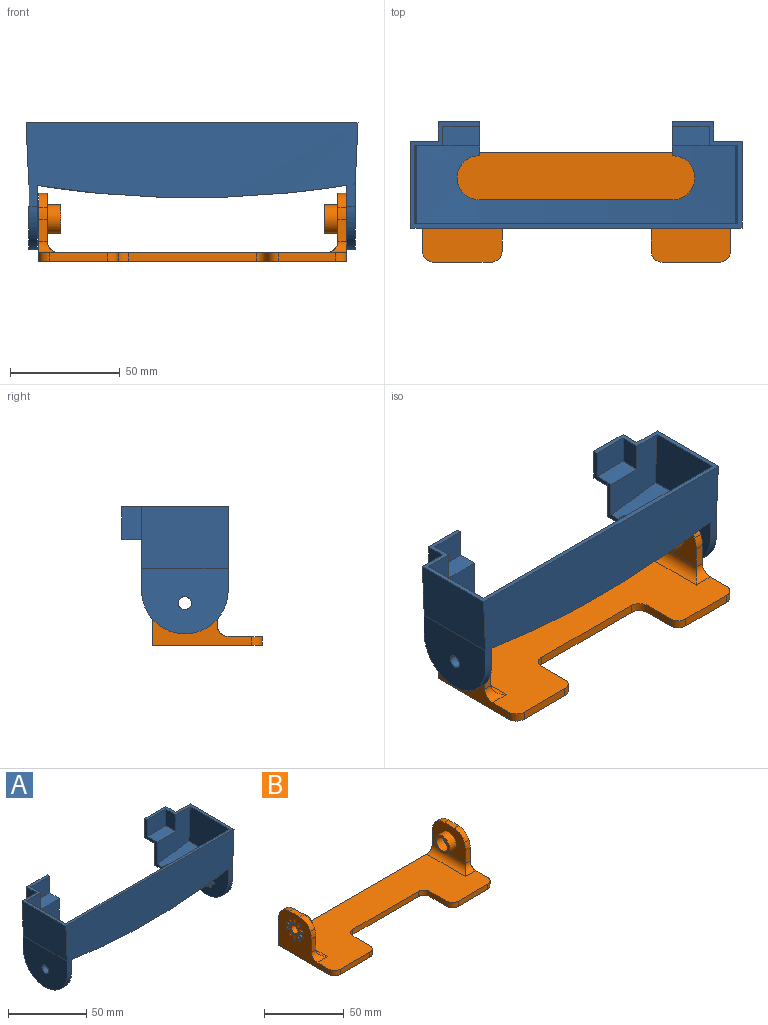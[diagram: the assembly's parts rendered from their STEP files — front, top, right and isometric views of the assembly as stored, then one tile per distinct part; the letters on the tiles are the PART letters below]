
ASSEMBLY  parts=2 mates=1
PART A: 142 faces, bbox 151.5x48.5x58 mm
  f0: cylinder r=443.67mm len=141mm, axis (0,1,0), area 2932.7mm2, adj f1,f32,f83,f84,f85,f86,f87,f88
  f1: plane 151.49x38.25mm, normal (0,-1,0), area 4905.7mm2, adj f0,f2,f21,f22,f23,f24,f26,f27
  f2: plane 151.49x48.5mm, normal (0,0,1), area 608.2mm2, adj f1,f3,f5,f7,f8,f10,f11,f12
  f3: plane 18.77x15mm, normal (0,1,0), area 281.5mm2, adj f2,f4,f20,f84
  f4: plane 18.77x9mm, normal (0,0,-1), area 168.9mm2, adj f3,f20,f83,f84
  f5: plane 16.77x13mm, normal (0,-1,0), area 218mm2, adj f2,f6,f7,f84
  f6: plane 16.77x9mm, normal (0,0,1), area 150.8mm2, adj f5,f7,f8,f84,f85
  f7: plane 13x9mm, normal (-1,0,0), area 117mm2, adj f2,f5,f6,f8
  f8: plane 30.03x29.76mm, normal (0,-1,0), area 605.6mm2, adj f2,f6,f7,f9,f10,f85
  f9: cylinder r=441.67mm len=145.15mm, axis (0,1,0), area 2691.9mm2, adj f8,f10,f11,f12,f13,f85,f86,f87
  f10: plane 35.5x26.2mm, normal (-1,0,0.04), area 931mm2, adj f2,f8,f9,f11
  f11: plane 147.48x32.25mm, normal (0,1,0), area 4422mm2, adj f2,f9,f10,f12
  f12: plane 35.5x26.3mm, normal (1,0,0.04), area 934.4mm2, adj f2,f9,f11,f13
  f13: plane 30.08x29.75mm, normal (0,-1,0), area 607.9mm2, adj f2,f9,f12,f14,f15,f89
  f14: plane 16.76x9mm, normal (0,0,1), area 150.8mm2, adj f13,f15,f16,f89
  f15: plane 13x9mm, normal (1,0,0), area 117mm2, adj f2,f13,f14,f16
  f16: plane 16.76x13mm, normal (0,-1,0), area 217.8mm2, adj f2,f14,f15,f89
  f17: plane 18.76x15mm, normal (0,1,0), area 281.3mm2, adj f2,f18,f19,f89
  f18: plane 18.76x9mm, normal (0,0,-1), area 168.8mm2, adj f17,f19,f89,f90
  f19: plane 15x9mm, normal (-1,0,0), area 135mm2, adj f2,f17,f18,f90
  f20: plane 15x9mm, normal (1,0,0), area 135mm2, adj f2,f3,f4,f83
  f21: plane 39.5x27.9mm, normal (1,0,-0.04), area 1103.2mm2, adj f1,f2,f22,f83
  f22: cylinder r=443.67mm len=39.5mm, axis (0,1,0), area 23.3mm2, adj f1,f21,f23,f83
  f23: plane 39.5x0.58mm, normal (0,0,1), area 23mm2, adj f1,f22,f24,f83
  f24: plane 39.5x30mm, normal (1,0,0), area 989.3mm2, adj f1,f23,f25,f26,f83
  f25: cylinder r=3mm len=6mm, axis (1,0,0), area 75.4mm2, adj f24,f32
  f26: cylinder r=19.75mm len=39.5mm, axis (1,0,0), area 248.2mm2, adj f1,f24,f32,f83
  f27: cylinder r=19.75mm len=39.5mm, axis (-1,0,0), area 248.2mm2, adj f1,f28,f90,f91
  f28: plane 39.5x30mm, normal (-1,0,0), area 989.3mm2, adj f1,f27,f29,f30,f90
  f29: cylinder r=3mm len=6mm, axis (-1,0,0), area 75.4mm2, adj f28,f91
  f30: plane 39.5x0mm, normal (0,0,1), area 0mm2, adj f28,f31
  f31: plane 39.5x28mm, normal (-1,0,-0.04), area 1107.1mm2, adj f1,f2,f30,f90
  f32: plane 39.5x29.43mm, normal (-1,0,0), area 904.1mm2, adj f0,f1,f25,f26,f33,f38,f43,f48
  f33: extruded ~4x2mm, area 1mm2, adj f32,f34,f35,f36,f37
  f34: bspline ~2x1.45mm, area 1.8mm2, adj f33,f35,f37
  f35: bspline ~3.07x1.23mm, area 2mm2, adj f33,f34,f36
  f36: bspline ~2x1.44mm, area 1.8mm2, adj f33,f35,f37
  f37: bspline ~3.1x1.26mm, area 2mm2, adj f33,f34,f36
  f38: extruded ~3.44x2.85mm, area 1mm2, adj f32,f39,f40,f41,f42
  f39: bspline ~1.73x1.43mm, area 1.8mm2, adj f38,f40,f42
  f40: bspline ~2.57x2.18mm, area 2mm2, adj f38,f39,f41
  f41: bspline ~1.73x1.43mm, area 1.8mm2, adj f38,f40,f42
  f42: bspline ~2.5x2.15mm, area 2mm2, adj f38,f39,f41
  f43: extruded ~3.85x2.27mm, area 1mm2, adj f32,f44,f45,f46,f47
  f44: bspline ~1.94x1.38mm, area 1.8mm2, adj f43,f45,f47
  f45: bspline ~2.9x1.68mm, area 2mm2, adj f43,f44,f46
  f46: bspline ~1.94x1.37mm, area 1.8mm2, adj f43,f45,f47
  f47: bspline ~2.77x1.63mm, area 2mm2, adj f43,f44,f46
  f48: extruded ~3.85x2.27mm, area 1mm2, adj f32,f49,f50,f51,f52
  f49: bspline ~1.94x1.38mm, area 1.8mm2, adj f48,f50,f52
  f50: bspline ~2.94x1.63mm, area 2mm2, adj f48,f49,f51
  f51: bspline ~1.94x1.37mm, area 1.8mm2, adj f48,f50,f52
  f52: bspline ~2.92x1.72mm, area 2mm2, adj f48,f49,f51
  f53: extruded ~3.44x2.85mm, area 1mm2, adj f32,f54,f55,f56,f57
  f54: bspline ~1.73x1.43mm, area 1.8mm2, adj f53,f55,f57
  f55: bspline ~2.57x2.22mm, area 2mm2, adj f53,f54,f56
  f56: bspline ~1.73x1.43mm, area 1.8mm2, adj f53,f55,f57
  f57: bspline ~2.62x2.17mm, area 2mm2, adj f53,f54,f56
  f58: extruded ~4x2mm, area 1mm2, adj f32,f59,f60,f61,f62
  f59: bspline ~2x1.45mm, area 1.8mm2, adj f58,f60,f62
  f60: bspline ~3.07x1.23mm, area 2mm2, adj f58,f59,f61
  f61: bspline ~2x1.44mm, area 1.8mm2, adj f58,f60,f62
  f62: bspline ~3.1x1.26mm, area 2mm2, adj f58,f59,f61
  f63: extruded ~3.44x2.85mm, area 1mm2, adj f32,f64,f65,f66,f67
  f64: bspline ~1.73x1.43mm, area 1.8mm2, adj f63,f65,f67
  f65: bspline ~2.57x2.18mm, area 2mm2, adj f63,f64,f66
  f66: bspline ~1.73x1.43mm, area 1.8mm2, adj f63,f65,f67
  f67: bspline ~2.58x2.26mm, area 2mm2, adj f63,f64,f66
  f68: extruded ~3.85x2.27mm, area 1mm2, adj f32,f69,f70,f71,f72
  f69: bspline ~1.94x1.38mm, area 1.8mm2, adj f68,f70,f72
  f70: bspline ~2.9x1.68mm, area 2mm2, adj f68,f69,f71
  f71: bspline ~1.94x1.37mm, area 1.8mm2, adj f68,f70,f72
  f72: bspline ~2.99x1.63mm, area 2mm2, adj f68,f69,f71
  f73: extruded ~3.85x2.27mm, area 1mm2, adj f32,f74,f75,f76,f77
  f74: bspline ~1.94x1.38mm, area 1.8mm2, adj f73,f75,f77
  f75: bspline ~2.94x1.63mm, area 2mm2, adj f73,f74,f76
  f76: bspline ~1.94x1.37mm, area 1.8mm2, adj f73,f75,f77
  f77: bspline ~2.92x1.72mm, area 2mm2, adj f73,f74,f76
  f78: extruded ~3.44x2.85mm, area 1mm2, adj f32,f79,f80,f81,f82
  f79: bspline ~1.73x1.43mm, area 1.8mm2, adj f78,f80,f82
  f80: bspline ~2.57x2.22mm, area 2mm2, adj f78,f79,f81
  f81: bspline ~1.73x1.43mm, area 1.8mm2, adj f78,f80,f82
  f82: bspline ~2.5x2.15mm, area 2mm2, adj f78,f79,f81
  f83: plane 38.25x31.76mm, normal (0,1,0), area 695.9mm2, adj f0,f2,f4,f20,f21,f22,f23,f24
  f84: plane 32.04x9mm, normal (-1,0,0), area 44mm2, adj f0,f2,f3,f4,f5,f6,f83,f85
  f85: plane 19.04x6.5mm, normal (-1,0,0), area 47.1mm2, adj f0,f6,f8,f9,f84,f86
  f86: cylinder r=10mm len=20mm, axis (0,0,1), area 65.1mm2, adj f0,f9,f85,f87
  f87: plane 87.83x4.19mm, normal (0,1,0), area 175.9mm2, adj f0,f9,f86,f88
  f88: cylinder r=10mm len=20mm, axis (0,0,1), area 63.8mm2, adj f0,f9,f87,f89
  f89: plane 32.09x15.5mm, normal (1,0,0), area 91.2mm2, adj f0,f2,f9,f13,f14,f16,f17,f18
  f90: plane 38.25x31.76mm, normal (0,1,0), area 698mm2, adj f0,f2,f18,f19,f27,f28,f31,f89
  f91: plane 39.5x29.34mm, normal (1,0,0), area 900.4mm2, adj f0,f1,f27,f29,f90,f92,f97,f102
  f92: extruded ~4x2mm, area 1mm2, adj f91,f93,f94,f95,f96
  f93: bspline ~3.07x1.23mm, area 2mm2, adj f92,f94,f96
  f94: bspline ~2x1.44mm, area 1.8mm2, adj f92,f93,f95
  f95: bspline ~3.1x1.26mm, area 2mm2, adj f92,f94,f96
  f96: bspline ~2x1.45mm, area 1.8mm2, adj f92,f93,f95
  f97: extruded ~3.44x2.85mm, area 1mm2, adj f91,f98,f99,f100,f101
  f98: bspline ~2.57x2.18mm, area 2mm2, adj f97,f99,f101
  f99: bspline ~1.73x1.43mm, area 1.8mm2, adj f97,f98,f100
  f100: bspline ~2.5x2.15mm, area 2mm2, adj f97,f99,f101
  f101: bspline ~1.73x1.43mm, area 1.8mm2, adj f97,f98,f100
  f102: extruded ~3.85x2.27mm, area 1mm2, adj f91,f103,f104,f105,f106
  f103: bspline ~2.9x1.68mm, area 2mm2, adj f102,f104,f106
  f104: bspline ~1.94x1.37mm, area 1.8mm2, adj f102,f103,f105
  f105: bspline ~2.77x1.63mm, area 2mm2, adj f102,f104,f106
  f106: bspline ~1.94x1.38mm, area 1.8mm2, adj f102,f103,f105
  f107: extruded ~3.85x2.27mm, area 1mm2, adj f91,f108,f109,f110,f111
  f108: bspline ~2.94x1.63mm, area 2mm2, adj f107,f109,f111
  f109: bspline ~1.94x1.37mm, area 1.8mm2, adj f107,f108,f110
  f110: bspline ~2.92x1.72mm, area 2mm2, adj f107,f109,f111
  f111: bspline ~1.94x1.38mm, area 1.8mm2, adj f107,f108,f110
  f112: extruded ~3.44x2.85mm, area 1mm2, adj f91,f113,f114,f115,f116
  f113: bspline ~2.57x2.22mm, area 2mm2, adj f112,f114,f116
  f114: bspline ~1.73x1.43mm, area 1.8mm2, adj f112,f113,f115
  f115: bspline ~2.62x2.17mm, area 2mm2, adj f112,f114,f116
  f116: bspline ~1.73x1.43mm, area 1.8mm2, adj f112,f113,f115
  f117: extruded ~4x2mm, area 1mm2, adj f91,f118,f119,f120,f121
  f118: bspline ~3.07x1.23mm, area 2mm2, adj f117,f119,f121
  f119: bspline ~2x1.44mm, area 1.8mm2, adj f117,f118,f120
  f120: bspline ~3.1x1.26mm, area 2mm2, adj f117,f119,f121
  f121: bspline ~2x1.45mm, area 1.8mm2, adj f117,f118,f120
  f122: extruded ~3.44x2.85mm, area 1mm2, adj f91,f123,f124,f125,f126
  f123: bspline ~2.57x2.18mm, area 2mm2, adj f122,f124,f126
  f124: bspline ~1.73x1.43mm, area 1.8mm2, adj f122,f123,f125
  f125: bspline ~2.58x2.26mm, area 2mm2, adj f122,f124,f126
  f126: bspline ~1.73x1.43mm, area 1.8mm2, adj f122,f123,f125
  f127: extruded ~3.85x2.27mm, area 1mm2, adj f91,f128,f129,f130,f131
  f128: bspline ~2.9x1.68mm, area 2mm2, adj f127,f129,f131
  f129: bspline ~1.94x1.37mm, area 1.8mm2, adj f127,f128,f130
  f130: bspline ~2.99x1.63mm, area 2mm2, adj f127,f129,f131
  f131: bspline ~1.94x1.38mm, area 1.8mm2, adj f127,f128,f130
  f132: extruded ~3.85x2.27mm, area 1mm2, adj f91,f133,f134,f135,f136
  f133: bspline ~2.94x1.63mm, area 2mm2, adj f132,f134,f136
  f134: bspline ~1.94x1.37mm, area 1.8mm2, adj f132,f133,f135
  f135: bspline ~2.92x1.72mm, area 2mm2, adj f132,f134,f136
  f136: bspline ~1.94x1.38mm, area 1.8mm2, adj f132,f133,f135
  f137: extruded ~3.44x2.85mm, area 1mm2, adj f91,f138,f139,f140,f141
  f138: bspline ~2.57x2.22mm, area 2mm2, adj f137,f139,f141
  f139: bspline ~1.73x1.43mm, area 1.8mm2, adj f137,f138,f140
  f140: bspline ~2.5x2.15mm, area 2mm2, adj f137,f139,f141
  f141: bspline ~1.73x1.43mm, area 1.8mm2, adj f137,f138,f140
PART B: 144 faces, bbox 140.5x50x31 mm
  f0: plane 10x10mm, normal (1,0,0), area 50.3mm2, adj f16,f141
  f1: plane 10x10mm, normal (-1,0,0), area 50.3mm2, adj f22,f138
  f2: plane 140.5x50mm, normal (0,0,1), area 4693.3mm2, adj f3,f4,f5,f6,f7,f8,f9,f10
  f3: plane 58x4mm, normal (0,-1,0), area 232mm2, adj f2,f11,f128,f133
  f4: plane 15x4mm, normal (-1,0,0), area 60mm2, adj f2,f11,f128,f129
  f5: plane 26.25x4mm, normal (0,-1,0), area 105mm2, adj f2,f11,f129,f130
  f6: plane 45x30.99mm, normal (1,0,0), area 841.2mm2, adj f2,f7,f11,f18,f19,f20,f21,f22
  f7: plane 140.5x19.24mm, normal (0,1,0), area 694.6mm2, adj f2,f6,f8,f11,f15,f17,f21,f23
  f8: plane 45x30.99mm, normal (-1,0,0), area 841.2mm2, adj f2,f7,f11,f12,f13,f14,f15,f16
  f9: plane 26.25x4mm, normal (0,-1,0), area 105mm2, adj f2,f11,f131,f132
  f10: plane 15x4mm, normal (1,0,0), area 60mm2, adj f2,f11,f132,f133
  f11: plane 140.5x50mm, normal (0,0,-1), area 5314.3mm2, adj f3,f4,f5,f6,f7,f8,f9,f10
  f12: plane 10.24x4mm, normal (0,-1,0), area 40.9mm2, adj f8,f13,f17,f127
  f13: cylinder r=14.75mm len=5.43mm, axis (1,0,0), area 22.3mm2, adj f8,f12,f17,f136
  f14: plane 8.83x4mm, normal (0,0,1), area 35.3mm2, adj f8,f17,f136,f137
  f15: cylinder r=14.75mm len=5.43mm, axis (1,0,0), area 22.3mm2, adj f7,f8,f17,f137
  f16: cylinder r=3mm len=6mm, axis (1,0,0), area 75.4mm2, adj f0,f8
  f17: plane 29.5x21.99mm, normal (1,0,0), area 466.7mm2, adj f7,f12,f13,f14,f15,f126,f136,f137
  f18: plane 10.24x4mm, normal (0,-1,0), area 40.9mm2, adj f6,f19,f23,f125
  f19: cylinder r=14.75mm len=5.43mm, axis (-1,0,0), area 22.3mm2, adj f6,f18,f23,f135
  f20: plane 8.83x4mm, normal (0,0,1), area 35.3mm2, adj f6,f23,f134,f135
  f21: cylinder r=14.75mm len=5.43mm, axis (-1,0,0), area 22.3mm2, adj f6,f7,f23,f134
  f22: cylinder r=3mm len=6mm, axis (-1,0,0), area 75.4mm2, adj f1,f6
  f23: plane 29.5x21.99mm, normal (-1,0,0), area 466.7mm2, adj f7,f18,f19,f20,f21,f124,f134,f135
  f24: extruded ~4x2mm, area 1mm2, adj f8,f70,f71,f72,f73
  f25: extruded ~3.44x2.85mm, area 1mm2, adj f8,f34,f35,f36,f37
  f26: extruded ~3.85x2.27mm, area 1mm2, adj f8,f38,f39,f40,f41
  f27: extruded ~3.85x2.27mm, area 1mm2, adj f8,f42,f43,f44,f45
  f28: extruded ~3.44x2.85mm, area 1mm2, adj f8,f46,f47,f48,f49
  f29: extruded ~4x2mm, area 1mm2, adj f8,f50,f51,f52,f53
  f30: extruded ~3.44x2.85mm, area 1mm2, adj f8,f54,f55,f56,f57
  f31: extruded ~3.85x2.27mm, area 1mm2, adj f8,f58,f59,f60,f61
  f32: extruded ~3.85x2.27mm, area 1mm2, adj f8,f62,f63,f64,f65
  f33: extruded ~3.44x2.85mm, area 1mm2, adj f8,f66,f67,f68,f69
  f34: bspline ~1.73x1.43mm, area 1.8mm2, adj f25,f35,f36
  f35: bspline ~2.57x2.18mm, area 2mm2, adj f25,f34,f37
  f36: bspline ~2.62x2.17mm, area 2mm2, adj f25,f34,f37
  f37: bspline ~1.73x1.43mm, area 1.8mm2, adj f25,f35,f36
  f38: bspline ~1.94x1.37mm, area 1.8mm2, adj f26,f39,f40
  f39: bspline ~2.89x1.68mm, area 2mm2, adj f26,f38,f41
  f40: bspline ~2.92x1.72mm, area 2mm2, adj f26,f38,f41
  f41: bspline ~1.94x1.38mm, area 1.8mm2, adj f26,f39,f40
  f42: bspline ~1.94x1.37mm, area 1.8mm2, adj f27,f43,f44
  f43: bspline ~2.94x1.63mm, area 2mm2, adj f27,f42,f45
  f44: bspline ~2.77x1.63mm, area 2mm2, adj f27,f42,f45
  f45: bspline ~1.94x1.38mm, area 1.8mm2, adj f27,f43,f44
  f46: bspline ~1.73x1.43mm, area 1.8mm2, adj f28,f47,f48
  f47: bspline ~2.57x2.22mm, area 2mm2, adj f28,f46,f49
  f48: bspline ~2.5x2.15mm, area 2mm2, adj f28,f46,f49
  f49: bspline ~1.73x1.43mm, area 1.8mm2, adj f28,f47,f48
  f50: bspline ~2x1.44mm, area 1.8mm2, adj f29,f51,f52
  f51: bspline ~3.07x1.23mm, area 2mm2, adj f29,f50,f53
  f52: bspline ~3.1x1.26mm, area 2mm2, adj f29,f50,f53
  f53: bspline ~2x1.45mm, area 1.8mm2, adj f29,f51,f52
  f54: bspline ~1.73x1.43mm, area 1.8mm2, adj f30,f55,f56
  f55: bspline ~2.57x2.18mm, area 2mm2, adj f30,f54,f57
  f56: bspline ~2.62x2.17mm, area 2mm2, adj f30,f54,f57
  f57: bspline ~1.73x1.43mm, area 1.8mm2, adj f30,f55,f56
  f58: bspline ~1.94x1.37mm, area 1.8mm2, adj f31,f59,f60
  f59: bspline ~2.89x1.68mm, area 2mm2, adj f31,f58,f61
  f60: bspline ~2.92x1.72mm, area 2mm2, adj f31,f58,f61
  f61: bspline ~1.94x1.38mm, area 1.8mm2, adj f31,f59,f60
  f62: bspline ~1.94x1.37mm, area 1.8mm2, adj f32,f63,f64
  f63: bspline ~2.94x1.63mm, area 2mm2, adj f32,f62,f65
  f64: bspline ~2.77x1.63mm, area 2mm2, adj f32,f62,f65
  f65: bspline ~1.94x1.38mm, area 1.8mm2, adj f32,f63,f64
  f66: bspline ~1.73x1.43mm, area 1.8mm2, adj f33,f67,f68
  f67: bspline ~2.57x2.22mm, area 2mm2, adj f33,f66,f69
  f68: bspline ~2.58x2.26mm, area 2mm2, adj f33,f66,f69
  f69: bspline ~1.73x1.43mm, area 1.8mm2, adj f33,f67,f68
  f70: bspline ~2x1.44mm, area 1.8mm2, adj f24,f71,f72
  f71: bspline ~3.07x1.23mm, area 2mm2, adj f24,f70,f73
  f72: bspline ~3.1x1.26mm, area 2mm2, adj f24,f70,f73
  f73: bspline ~2x1.45mm, area 1.8mm2, adj f24,f71,f72
  f74: extruded ~3.85x2.27mm, area 1mm2, adj f6,f120,f121,f122,f123
  f75: extruded ~3.44x2.85mm, area 1mm2, adj f6,f84,f85,f86,f87
  f76: extruded ~3.85x2.27mm, area 1mm2, adj f6,f116,f117,f118,f119
  f77: extruded ~3.44x2.85mm, area 1mm2, adj f6,f112,f113,f114,f115
  f78: extruded ~4x2mm, area 1mm2, adj f6,f108,f109,f110,f111
  f79: extruded ~3.44x2.85mm, area 1mm2, adj f6,f104,f105,f106,f107
  f80: extruded ~3.85x2.27mm, area 1mm2, adj f6,f100,f101,f102,f103
  f81: extruded ~3.85x2.27mm, area 1mm2, adj f6,f96,f97,f98,f99
  f82: extruded ~3.44x2.85mm, area 1mm2, adj f6,f92,f93,f94,f95
  f83: extruded ~4x2mm, area 1mm2, adj f6,f88,f89,f90,f91
  f84: bspline ~1.73x1.43mm, area 1.8mm2, adj f75,f85,f86
  f85: bspline ~2.57x2.18mm, area 2mm2, adj f75,f84,f87
  f86: bspline ~2.62x2.17mm, area 2mm2, adj f75,f84,f87
  f87: bspline ~1.73x1.43mm, area 1.8mm2, adj f75,f85,f86
  f88: bspline ~2x1.44mm, area 1.8mm2, adj f83,f89,f90
  f89: bspline ~3.07x1.23mm, area 2mm2, adj f83,f88,f91
  f90: bspline ~3.1x1.26mm, area 2mm2, adj f83,f88,f91
  f91: bspline ~2x1.45mm, area 1.8mm2, adj f83,f89,f90
  f92: bspline ~1.73x1.43mm, area 1.8mm2, adj f82,f93,f94
  f93: bspline ~2.57x2.22mm, area 2mm2, adj f82,f92,f95
  f94: bspline ~2.5x2.15mm, area 2mm2, adj f82,f92,f95
  f95: bspline ~1.73x1.43mm, area 1.8mm2, adj f82,f93,f94
  f96: bspline ~1.94x1.37mm, area 1.8mm2, adj f81,f97,f98
  f97: bspline ~2.94x1.63mm, area 2mm2, adj f81,f96,f99
  f98: bspline ~2.99x1.63mm, area 2mm2, adj f81,f96,f99
  f99: bspline ~1.94x1.38mm, area 1.8mm2, adj f81,f97,f98
  f100: bspline ~1.94x1.37mm, area 1.8mm2, adj f80,f101,f102
  f101: bspline ~2.89x1.68mm, area 2mm2, adj f80,f100,f103
  f102: bspline ~2.92x1.72mm, area 2mm2, adj f80,f100,f103
  f103: bspline ~1.94x1.38mm, area 1.8mm2, adj f80,f101,f102
  f104: bspline ~1.73x1.43mm, area 1.8mm2, adj f79,f105,f106
  f105: bspline ~2.57x2.18mm, area 2mm2, adj f79,f104,f107
  f106: bspline ~2.62x2.17mm, area 2mm2, adj f79,f104,f107
  f107: bspline ~1.73x1.43mm, area 1.8mm2, adj f79,f105,f106
  f108: bspline ~2x1.44mm, area 1.8mm2, adj f78,f109,f110
  f109: bspline ~3.07x1.23mm, area 2mm2, adj f78,f108,f111
  f110: bspline ~3.1x1.26mm, area 2mm2, adj f78,f108,f111
  f111: bspline ~2x1.45mm, area 1.8mm2, adj f78,f109,f110
  f112: bspline ~1.73x1.43mm, area 1.8mm2, adj f77,f113,f114
  f113: bspline ~2.57x2.22mm, area 2mm2, adj f77,f112,f115
  f114: bspline ~2.58x2.26mm, area 2mm2, adj f77,f112,f115
  f115: bspline ~1.73x1.43mm, area 1.8mm2, adj f77,f113,f114
  f116: bspline ~1.94x1.37mm, area 1.8mm2, adj f76,f117,f118
  f117: bspline ~2.94x1.63mm, area 2mm2, adj f76,f116,f119
  f118: bspline ~2.99x1.63mm, area 2mm2, adj f76,f116,f119
  f119: bspline ~1.94x1.38mm, area 1.8mm2, adj f76,f117,f118
  f120: bspline ~1.94x1.37mm, area 1.8mm2, adj f74,f121,f122
  f121: bspline ~2.89x1.68mm, area 2mm2, adj f74,f120,f123
  f122: bspline ~2.92x1.72mm, area 2mm2, adj f74,f120,f123
  f123: bspline ~1.94x1.38mm, area 1.8mm2, adj f74,f121,f122
  f124: cylinder r=5mm len=34.5mm, axis (0,1,0), area 251.3mm2, adj f2,f7,f23,f125
  f125: cylinder r=5mm len=9mm, axis (-1,0,0), area 51.1mm2, adj f2,f6,f18,f124
  f126: cylinder r=5mm len=34.5mm, axis (0,-1,0), area 251.3mm2, adj f2,f7,f17,f127
  f127: cylinder r=5mm len=9mm, axis (-1,0,0), area 51.1mm2, adj f2,f8,f12,f126
  f128: cylinder r=5mm len=5mm, axis (0,0,1), area 31.4mm2, adj f2,f3,f4,f11
  f129: cylinder r=5mm len=5mm, axis (0,0,1), area 31.4mm2, adj f2,f4,f5,f11
  f130: cylinder r=5mm len=5mm, axis (0,0,1), area 31.4mm2, adj f2,f5,f6,f11
  f131: cylinder r=5mm len=5mm, axis (0,0,-1), area 31.4mm2, adj f2,f8,f9,f11
  f132: cylinder r=5mm len=5mm, axis (0,0,-1), area 31.4mm2, adj f2,f9,f10,f11
  f133: cylinder r=5mm len=5mm, axis (0,0,-1), area 31.4mm2, adj f2,f3,f10,f11
  f134: cylinder r=10mm len=9.3mm, axis (-1,0,0), area 47.7mm2, adj f6,f20,f21,f23
  f135: cylinder r=10mm len=9.3mm, axis (-1,0,0), area 47.7mm2, adj f6,f19,f20,f23
  f136: cylinder r=10mm len=9.3mm, axis (1,0,0), area 47.7mm2, adj f8,f13,f14,f17
  f137: cylinder r=10mm len=9.3mm, axis (1,0,0), area 47.7mm2, adj f8,f14,f15,f17
  f138: cylinder r=5mm len=10mm, axis (1,0,0), area 188.5mm2, adj f1,f140
  f139: cylinder r=6.5mm len=13mm, axis (1,0,0), area 245mm2, adj f23,f140
  f140: plane 13x13mm, normal (-1,0,0), area 54.2mm2, adj f138,f139
  f141: cylinder r=5mm len=10mm, axis (-1,0,0), area 188.5mm2, adj f0,f143
  f142: cylinder r=6.5mm len=13mm, axis (-1,0,0), area 245mm2, adj f17,f143
  f143: plane 13x13mm, normal (1,0,0), area 54.2mm2, adj f141,f142
PLACE A t=(-56.78,33.72,77.35)mm
PLACE B t=(-56.53,-5.28,-5.63)mm
MATE revolute A.f25 <-> B.f138  axis (-1,0,0) through (13.72,4.97,13.6)mm
